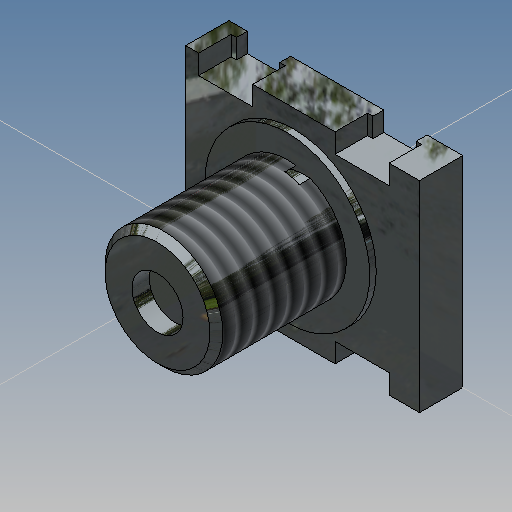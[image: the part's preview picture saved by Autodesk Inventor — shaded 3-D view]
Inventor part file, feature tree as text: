
AUTODESK INVENTOR PART (.ipt)
format: ipt  version: 2019 (Build 230136000, 136)  size: 344,576 bytes
history: native  units: in
note: dims shown in document units (in); Inventor stores cm internally (conversion verified against a paired STEP export)
features: sketch x9, extrude x8, reference x2, thread x1, chamfer x1, plane x1, revolve x1
ambient origin geometry x8: Origin, YZ Plane, XZ Plane, XY Plane, X Axis, Y Axis, Z Axis, Center Point
bodies: Solid1 (feature_tree)
feature tree (23):
  extrude  "Extrusion1"  Depth=0.464in
  extrude  "Extrusion2"  Depth=0.1in
  thread  "Thread1"  [1 undecoded]
  extrude  "Extrusion3"  Depth=0.315in
  chamfer  "Chamfer1"  Distance=0.315in
  plane  "Work Plane1"
  revolve  "Revolution1"  [1 undecoded]
  extrude  "Extrusion4"  Depth=0.015in TaperAngle=45.0deg
  extrude  "Extrusion5"  Depth=0.01in
  extrude  "Extrusion6"  TaperAngle=90.0deg  [1 undecoded]
  extrude  "Extrusion7"  Depth=0.04in TaperAngle=0.0deg
  extrude  "Extrusion8"  Depth=0.125in
  sketch  "Sketch1"  dims[d0=0.54in d1=0.464in]
  sketch  "Sketch2"  dims[d2=0.1in d3=0.0in d4=0.272in d5=0.29in]
  sketch  "Sketch3"  dims[d6=0.464in d7=0.232in d8=0.315in d9=0.0in]
  sketch  "Sketch4"  dims[d10=1.0in d11=0.0in d12=0.38in]
  sketch  "Sketch5"  dims[d13=0.015in d14=0.0in d15=0.015in d16=0.125in d17=45.0deg]
  sketch  "Sketch6"  dims[d18=0.29in d19=0.01in]
  reference  "Reference1"
  reference  "Reference2"
  sketch  "Sketch7"  dims[d20=0.025in d21=90.0deg]
  sketch  "Sketch8"  dims[d22=0.118in d23=0.04in d24=0.0in]
  sketch  "Sketch9"  dims[d25=0.125in d26=0.125in d27=0.125in d28=0.125in d29=0.54in d30=0.44in d32=0.045in d33=0.045in d34=0.19in d35=0.03in d36=0.075in d37=0.0in d38=0.125in d39=0.1in d40=0.0125in d41=0.075in d42=0.0in d43=0.1in d44=0.125in d45=0.0125in d46=0.075in d47=0.0in d48=0.1in d49=0.125in d50=0.0125in d51=0.0125in d52=0.075in d53=0.0in]
note: 3 required parameter values undecoded (feature->parameter linkage not recoverable at this tier; creation-order binding heuristic only, values carry confidence <= 0.55)